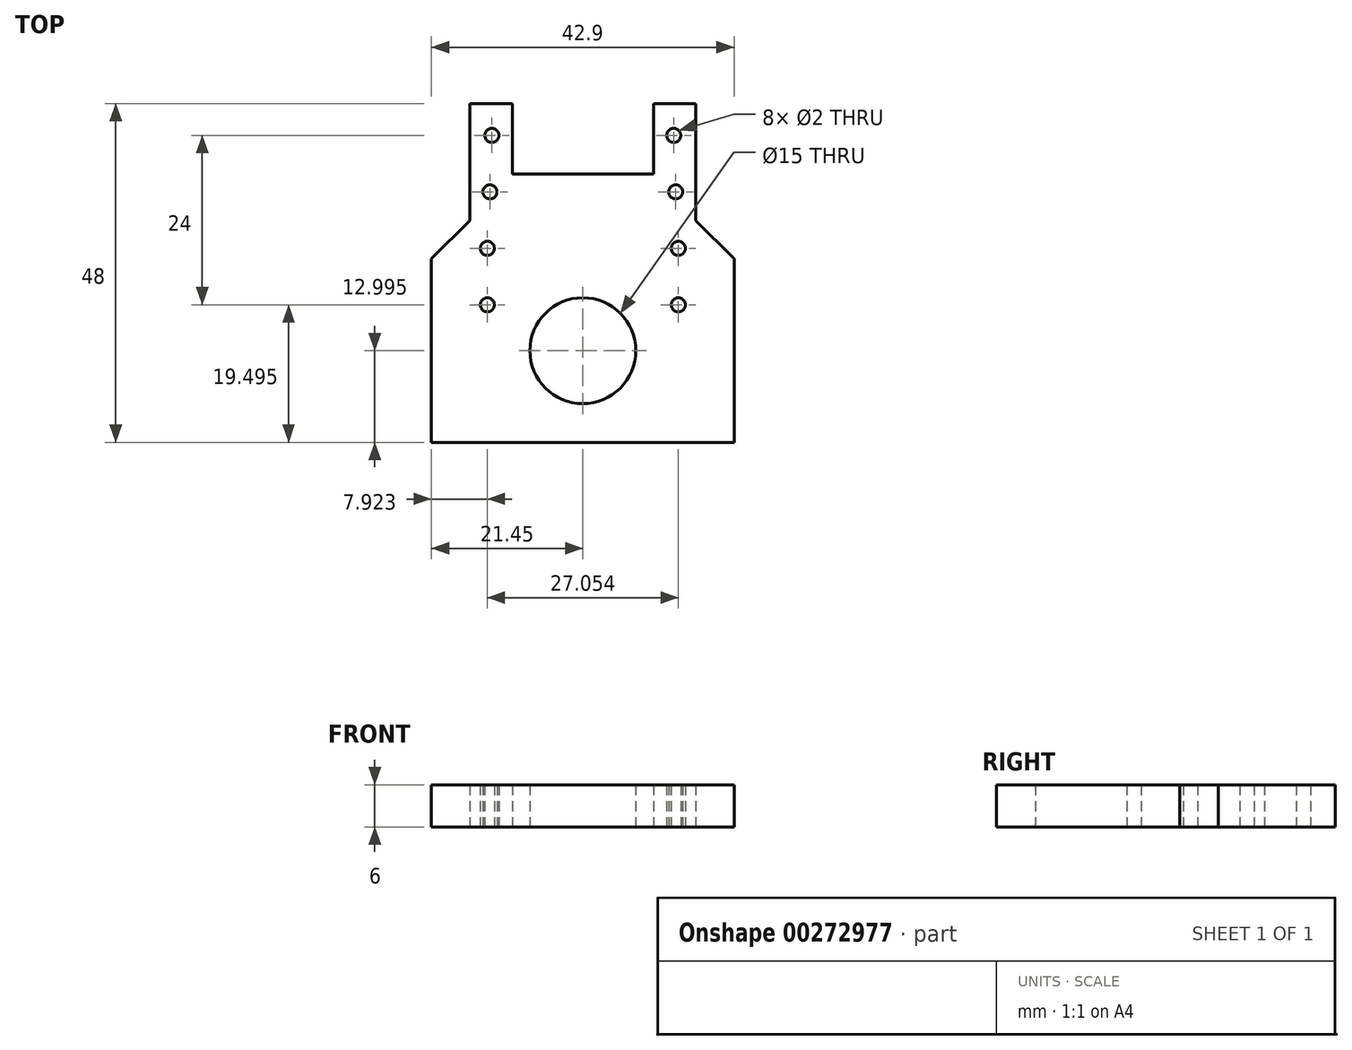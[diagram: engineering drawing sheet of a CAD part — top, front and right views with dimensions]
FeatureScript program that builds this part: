
annotation { "Feature Type Name" : "Feature", "Feature Type Description" : "" }
export const myFeature = defineFeature(function(context is Context, id is Id, definition is map)
    precondition{}
    {
        {
            var Q0;
            Q0=qCreatedBy(makeId("Top.planeOp"),FACE);
            var sketch = newSketch(context, id + "F0", { "sketchPlane" : qUnion([Q0])});
            skLineSegment(sketch, "E0.bottom", {"start": v(-16, 36.18) * mm, "end": v(-10, 36.18) * mm});
            skLineSegment(sketch, "E0.top", {"start": v(-21.45, -11.82) * mm, "end": v(21.45, -11.82) * mm});
            skLineSegment(sketch, "E0.left", {"start": v(-21.45, 14.18) * mm, "end": v(-21.45, -11.82) * mm});
            skLineSegment(sketch, "E0.right", {"start": v(21.45, 14.18) * mm, "end": v(21.45, -11.82) * mm});
            skCircle(sketch, "E1", {"center": v(0, 1.18) * mm, "radius": 7.5 * mm});
            skLineSegment(sketch, "E2.top", {"start": v(-21.45, 14.18) * mm, "end": v(-16, 14.18) * mm, "construction": true});
            skLineSegment(sketch, "E2.right", {"start": v(-16, 36.18) * mm, "end": v(-16, 19.63) * mm});
            skLineSegment(sketch, "E3.top", {"start": v(21.45, 14.18) * mm, "end": v(16, 14.18) * mm, "construction": true});
            skLineSegment(sketch, "E3.right", {"start": v(16, 36.18) * mm, "end": v(16, 19.63) * mm});
            skLineSegment(sketch, "E4", {"start": v(-21.45, 14.18) * mm, "end": v(-16, 19.63) * mm});
            skLineSegment(sketch, "E5", {"start": v(21.45, 14.18) * mm, "end": v(16, 19.63) * mm});
            skLineSegment(sketch, "E6", {"start": v(-16, 19.63) * mm, "end": v(-16, 14.18) * mm, "construction": true});
            skLineSegment(sketch, "E7", {"start": v(16, 19.63) * mm, "end": v(16, 14.18) * mm, "construction": true});
            skCircle(sketch, "E8", {"center": v(-12.89, 31.68) * mm, "radius": 1 * mm});
            skCircle(sketch, "E9", {"center": v(-13.16, 23.68) * mm, "radius": 1 * mm});
            skCircle(sketch, "E10", {"center": v(-13.53, 15.68) * mm, "radius": 1 * mm});
            skLineSegment(sketch, "E11", {"start": v(-10, 36.18) * mm, "end": v(-10, 26.18) * mm});
            skLineSegment(sketch, "E12", {"start": v(-10, 26.18) * mm, "end": v(10, 26.18) * mm});
            skLineSegment(sketch, "E13", {"start": v(10, 26.18) * mm, "end": v(10, 36.18) * mm});
            skLineSegment(sketch, "E14", {"start": v(-10, 36.18) * mm, "end": v(10, 36.18) * mm, "construction": true});
            skLineSegment(sketch, "E15", {"start": v(10, 36.18) * mm, "end": v(16, 36.18) * mm});
            skCircle(sketch, "E16", {"center": v(-13.53, 7.68) * mm, "radius": 1 * mm});
            skCircle(sketch, "E17.MirrorC", {"center": v(12.89, 31.68) * mm, "radius": 1 * mm});
            skCircle(sketch, "E18.MirrorC", {"center": v(13.16, 23.68) * mm, "radius": 1 * mm});
            skCircle(sketch, "E19.MirrorC", {"center": v(13.53, 15.68) * mm, "radius": 1 * mm});
            skCircle(sketch, "E20.MirrorC", {"center": v(13.53, 7.68) * mm, "radius": 1 * mm});
            skSolve(sketch);
        }
        {
            var Q0;
            Q0 = qSketchRegion(id + "F0", true);
            extrude(context, id + "F1", {"entities" : qUnion([Q0]), "depth" : 6 * mm});
        }
    });
